# Revit family: Турникет тумбовый PERCo_TTD-08A
name_source: partatom
category: Оборудование
units: mm (PartAtom-declared; Revit-internal decimal feet)

## family parameters
Всегда вертикально = Нет
Классификация = Нет
На основе рабочей плоскости = Нет
Общий = Нет
При загрузке вырезать с полостями = Нет
Размер круглого соединителя = Использовать диаметр
Тип детали = Нормальный
Точка расчета площади = Нет

## types (1)
- TTD-08A
    ADSK_URL страницы изделия = https://www.perco.ru
    ADSK_Единица измерения = шт.
    ADSK_Завод-изготовитель = PERCo
    ADSK_Количество = 1
    ADSK_Масса_Текст = не более 70 кг
    ADSK_Материал наименование = Корпус турникета выполнен из высококачественной нержавеющей стали со вставками из АБС-пластика, планки из нержавеющей стали
    ADSK_Наименование = Турникет тумбовый PERCo-TTD-08A с автоматическими преграждающими планками Антипаника
    ADSK_Наименование краткое = Турникет тумбовый TTD-08A
    ADSK_Напряжение = 12 В
    ADSK_Номинальная мощность = 72 Вт
    ADSK_Ток = 6 А
    Встраивание считывателей внутрь = Нет
    Габаритные размеры (длина×ширина×высота) = 1166×750×1016 мм
    Габаритные размеры контроллера для встраивания в нишу = не более 135×90×30 мм
    Габаритные размеры считывателя для встраивания в ниши = не более 250×130×35 мм
    Длина планки = 567 мм
    Емкость картоприёмника = Не предусмотрено
    Корпус = Нержавейка
    Крышка_вставки = Пластик черный
    Основание планки = Черный
    Планки = Нержавейка
    Подключение к электросети = 220 В
    Пропускная способность = 30 чел./мин
    Степень защиты оболочки = IP54
    Температура использования = от -20°С до +50°С
    Ширина зоны прохода = 560 мм.
